# Revit family: Marco - 2225 Rectangle 54x24
name_source: partatom
category: Furniture
units: mm (PartAtom-declared; Revit-internal decimal feet)

## family parameters
Always vertical = Yes
Cut with Voids When Loaded = No
OmniClass Number = 23.40.20.00
OmniClass Title = General Furniture and Specialties
Room Calculation Point = No
Shared = No
Work Plane-Based = No

## types (6) — shared parameters
Manufacturer = Marco Group
Model = Marco-2225
Type Image = <None>
URL = https://www.madebymarco.net
zero-valued in all types: Default Elevation

## per-type parameters (varying)
| type | Appex leg A | Appex leg B | Leg type | MG leg A | MG leg B | Premier leg A | Premier leg B |
| 43-2225-A | No | No | Marco - All leg types : Marco - Premier Leg A | No | No | Yes | No |
| 38-2225-B | No | Yes | Marco - All leg types : Marco - Appex Leg B | No | No | No | No |
| 43-2225-B | No | No | Marco - All leg types : Marco - Premier Leg B | No | No | No | Yes |
| 38-2225-A | Yes | No | Marco - All leg types : Marco - Appex Leg A | No | No | No | No |
| MG2225-A | No | No | Marco - All leg types : Marco - MG leg A | Yes | No | No | No |
| MG2225-B | No | No | Marco - All leg types : Marco - MG leg B | No | Yes | No | No |

## geometry (parser evidence)
native form markers: Sweep x26
no freeform markers — native parametric forms only
